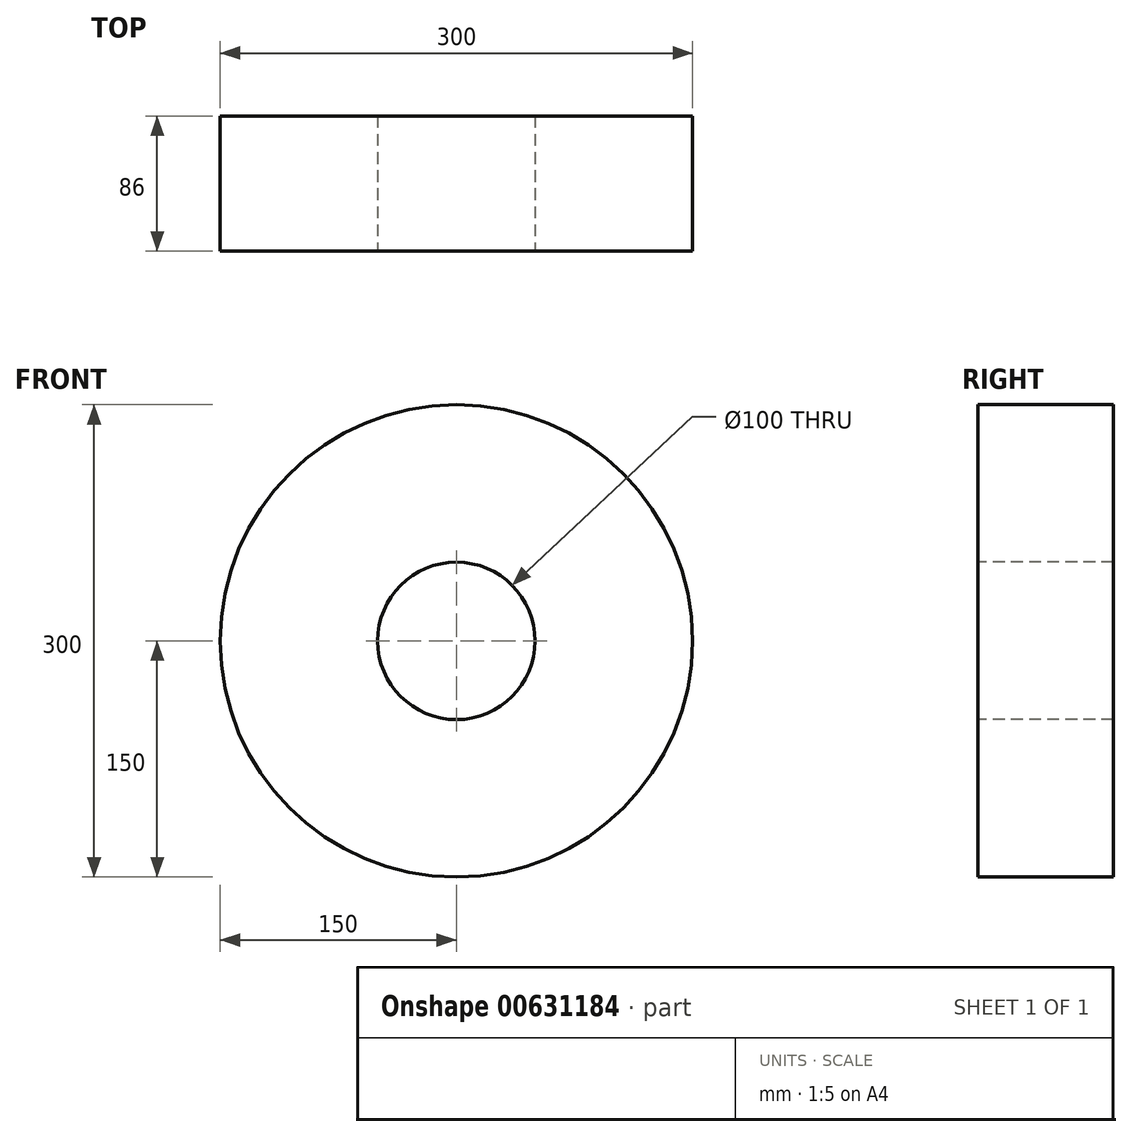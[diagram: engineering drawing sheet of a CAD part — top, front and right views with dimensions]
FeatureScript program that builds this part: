
annotation { "Feature Type Name" : "Feature", "Feature Type Description" : "" }
export const myFeature = defineFeature(function(context is Context, id is Id, definition is map)
    precondition{}
    {
        {
            var Q0;
            Q0=qCreatedBy(makeId("Right.planeOp"),FACE);
            var sketch = newSketch(context, id + "F0", { "sketchPlane" : qUnion([Q0])});
            skLineSegment(sketch, "E0", {"start": v(0, 50) * mm, "end": v(-86, 50) * mm});
            skLineSegment(sketch, "E1", {"start": v(-86, 50) * mm, "end": v(-86, 150) * mm});
            skLineSegment(sketch, "E2", {"start": v(-86, 150) * mm, "end": v(0, 150) * mm});
            skLineSegment(sketch, "E3", {"start": v(0, 150) * mm, "end": v(0, 50) * mm});
            skLineSegment(sketch, "E4", {"start": v(0, 0) * mm, "end": v(13.98, 0) * mm, "construction": true});
            skSolve(sketch);
        }
        {
            var Q0;
            Q0=makeQuery(id+"F0.imprint","IMPRINT",FACE,{"disambiguationData":[TD([[makeQuery(id+"F0.imprint","IMPRINT",EDGE,{"derivedFrom":sQuery(id+"F0.wireOp",EDGE,"E0")}),-1.0]])]});
            var Q1;
            Q1=sQuery(id+"F0.wireOp",EDGE,"E4");
            revolve(context, id + "F1", {"entities" : qUnion([Q0]), "axis" : qUnion([Q1]), "revolveType" : RevolveType.FULL});
        }
    });
